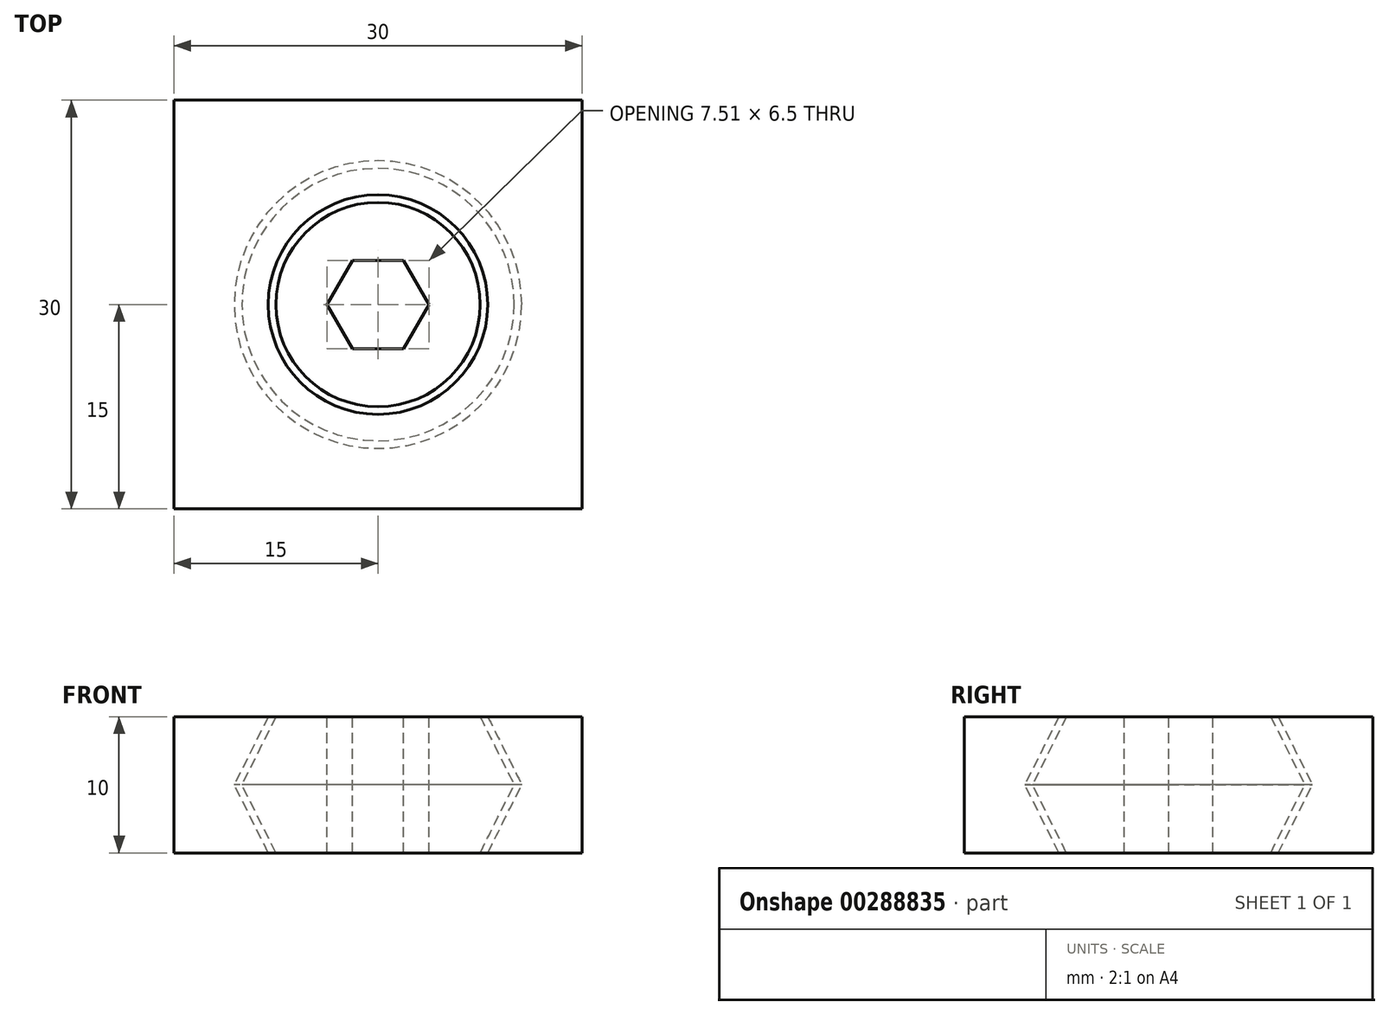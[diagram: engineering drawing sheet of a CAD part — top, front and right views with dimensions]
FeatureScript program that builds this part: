
annotation { "Feature Type Name" : "Feature", "Feature Type Description" : "" }
export const myFeature = defineFeature(function(context is Context, id is Id, definition is map)
    precondition{}
    {
        {
            var Q0;
            Q0=qCreatedBy(makeId("Top.planeOp"),FACE);
            cPlane(context, id + "F0", {"entities" : qUnion([Q0]), "cplaneType" : CPlaneType.OFFSET, "offset" : 5 * mm, "width" : 150 * mm, "height" : 150 * mm});
        }
        {
            var Q0;
            Q0=qCreatedBy(makeId("Top.planeOp"),FACE);
            var sketch = newSketch(context, id + "F1", { "sketchPlane" : qUnion([Q0])});
            skLineSegment(sketch, "E0.bottom", {"start": v(15, -15) * mm, "end": v(-15, -15) * mm});
            skLineSegment(sketch, "E0.top", {"start": v(15, 15) * mm, "end": v(-15, 15) * mm});
            skLineSegment(sketch, "E0.left", {"start": v(15, -15) * mm, "end": v(15, 15) * mm});
            skLineSegment(sketch, "E0.right", {"start": v(-15, -15) * mm, "end": v(-15, 15) * mm});
            skPoint(sketch, "E0.middle", {"position": v(0, 0) * mm});
            skCircle(sketch, "E1", {"center": v(0, 0) * mm, "radius": 10 * mm});
            skSolve(sketch);
        }
        {
            var Q0;
            Q0=qCreatedBy(id+"F0.planeOp",FACE);
            var sketch = newSketch(context, id + "F2", { "sketchPlane" : qUnion([Q0])});
            skCircle(sketch, "E2", {"center": v(0, 0) * mm, "radius": 7.5 * mm});
            skSolve(sketch);
        }
        {
            var Q0;
            Q0=makeQuery(id+"F1.imprint","IMPRINT",FACE,{"disambiguationData":[TD([[makeQuery(id+"F1.imprint","IMPRINT",EDGE,{"derivedFrom":sQuery(id+"F1.wireOp",EDGE,"E1")}),1.0]])]});
            var Q1;
            Q1=makeQuery(id+"F2.imprint","IMPRINT",FACE,{"disambiguationData":[TD([[makeQuery(id+"F2.imprint","IMPRINT",EDGE,{"derivedFrom":sQuery(id+"F2.wireOp",EDGE,"E2")}),1.0]])]});
            loft(context, id + "F3", {"sheetProfilesArray" : [{ "sheetProfileEntities" : qUnion([Q0]) }, { "sheetProfileEntities" : qUnion([Q1]) }]});
        }
        {
            var Q0;
            Q0=makeQuery(id+"F3.opLoft","SWEPT_BODY",BODY,{"disambiguationData":[OSD([makeQuery(id+"F1.imprint","IMPRINT",FACE,{"disambiguationData":[TD([[makeQuery(id+"F1.imprint","IMPRINT",EDGE,{"derivedFrom":sQuery(id+"F1.wireOp",EDGE,"E1")}),1.0]])]}),makeQuery(id+"F2.imprint","IMPRINT",FACE,{"disambiguationData":[TD([[makeQuery(id+"F2.imprint","IMPRINT",EDGE,{"derivedFrom":sQuery(id+"F2.wireOp",EDGE,"E2")}),1.0]])]})])]});
            var Q1;
            Q1=qCreatedBy(makeId("Top.planeOp"),FACE);
            mirror(context, id + "F4", {"operationType" : NewBodyOperationType.ADD, "entities" : qUnion([Q0]), "mirrorPlane" : qUnion([Q1])});
        }
        {
            var Q0;
            Q0=makeQuery(id+"F1.imprint","IMPRINT",FACE,{"disambiguationData":[TD([[makeQuery(id+"F1.imprint","IMPRINT",EDGE,{"derivedFrom":sQuery(id+"F1.wireOp",EDGE,"E0.bottom")}),-1.0]])]});
            var Q1;
            Q1=makeQuery(id+"F1.imprint","IMPRINT",FACE,{"disambiguationData":[TD([[makeQuery(id+"F1.imprint","IMPRINT",EDGE,{"derivedFrom":sQuery(id+"F1.wireOp",EDGE,"E1")}),1.0]])]});
            extrude(context, id + "F5", {"entities" : qUnion([Q0, Q1]), "endBound" : BoundingType.SYMMETRIC, "depth" : 10 * mm});
        }
        {
            var Q0;
            Q0=makeQuery(id+"F3.opLoft","SWEPT_BODY",BODY,{"disambiguationData":[OSD([makeQuery(id+"F1.imprint","IMPRINT",FACE,{"disambiguationData":[TD([[makeQuery(id+"F1.imprint","IMPRINT",EDGE,{"derivedFrom":sQuery(id+"F1.wireOp",EDGE,"E1")}),1.0]])]}),makeQuery(id+"F2.imprint","IMPRINT",FACE,{"disambiguationData":[TD([[makeQuery(id+"F2.imprint","IMPRINT",EDGE,{"derivedFrom":sQuery(id+"F2.wireOp",EDGE,"E2")}),1.0]])]})])]});
            var Q1;
            Q1=makeQuery(id+"F5.opExtrude","SWEPT_BODY",BODY,{"disambiguationData":[OSD([sQuery(id+"F1.wireOp",EDGE,"E0.bottom"),sQuery(id+"F1.wireOp",EDGE,"E0.top"),sQuery(id+"F1.wireOp",EDGE,"E0.left"),sQuery(id+"F1.wireOp",EDGE,"E0.right")])]});
            booleanBodies(context, id + "F6", {"operationType" : BooleanOperationType.SUBTRACTION, "tools" : qUnion([Q0]), "targets" : qUnion([Q1]), "offset" : true, "offsetAll" : true, "offsetDistance" : 0.5 * mm, "keepTools" : true});
        }
        {
            var Q0;
            Q0=qCreatedBy(makeId("Top.planeOp"),FACE);
            var sketch = newSketch(context, id + "F7", { "sketchPlane" : qUnion([Q0])});
            skCircle(sketch, "E3.cCircle", {"center": v(0, 0) * mm, "radius": 3.25 * mm, "construction": true});
            skLineSegment(sketch, "E3.0", {"start": v(-1.88, 3.25) * mm, "end": v(1.88, 3.25) * mm});
            skLineSegment(sketch, "E3.1", {"start": v(1.88, 3.25) * mm, "end": v(3.75, 0) * mm});
            skLineSegment(sketch, "E3.2", {"start": v(3.75, 0) * mm, "end": v(1.88, -3.25) * mm});
            skLineSegment(sketch, "E3.3", {"start": v(1.88, -3.25) * mm, "end": v(-1.88, -3.25) * mm});
            skLineSegment(sketch, "E3.4", {"start": v(-1.88, -3.25) * mm, "end": v(-3.75, 0) * mm});
            skLineSegment(sketch, "E3.5", {"start": v(-3.75, 0) * mm, "end": v(-1.88, 3.25) * mm});
            skPoint(sketch, "E3.0.midPoint", {"position": v(0, 3.25) * mm});
            skSolve(sketch);
        }
        {
            var Q0;
            Q0=makeQuery(id+"F7.imprint","IMPRINT",FACE,{"disambiguationData":[TD([[makeQuery(id+"F7.imprint","IMPRINT",EDGE,{"derivedFrom":sQuery(id+"F7.wireOp",EDGE,"E3.0")}),-1.0]])]});
            extrude(context, id + "F8", {"entities" : qUnion([Q0]), "operationType" : NewBodyOperationType.REMOVE, "endBound" : BoundingType.SYMMETRIC, "oppositeDirection" : true, "depth" : 25 * mm});
        }
    });
